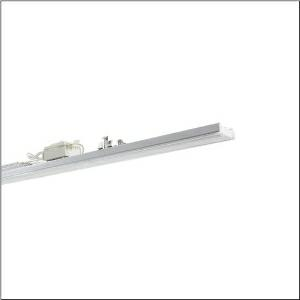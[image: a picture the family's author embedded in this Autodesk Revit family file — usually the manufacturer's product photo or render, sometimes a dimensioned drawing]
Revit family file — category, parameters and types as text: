
# Revit family: licross_r__21_recessed_mo_52tl127n44xg_e1cf
name_source: partatom
category: Lighting Fixtures
units: mm (PartAtom-declared; Revit-internal decimal feet)

## family parameters
Cut with Voids When Loaded = No
Host = Face
Light Source = No
Part Type = Normal
Room Calculation Point = No
Round Connector Dimension = Use Diameter
Shared = No

## types (1)
- Licross® 21 Recessed MO (1 x LED, 4160 lm, 22.2 W, 4000K)
    Apparent Load = 22 VA
    CIE Flux Codes = 72 92 99 100 100
    Color Rendering = 80
    Color Temperature = 4000K
    Default Elevation = 1800 mm
    Description = Licross® 21 Recessed MO, luminaire insert, of sheet steel, galvanised, coil coated, white, length: 1.500mm, width: 66mm, height: 67mm, LED rated luminous flux: 4.160lm, light colour: 840, control gear: ON/OFF, control gear: ECG, with plug, 3-pole, with phase selection, mains connection: 220..240V, AC, 50/60Hz, rated input power: 22W, halogen-free wiring, primary optical cover: cover, of PMMA, light emission: direct distribution, primary light characteristic: symmetric, protection rating (complete): IP40, insulation class (complete): insulation class I (protective earthing), certification: CE, ENEC, VDE, UKCA, protection symbol: D if used in an environment without relevant dust loads with corresponding accessories, impact resistance: IK06, permissible ambient temperature for indoor applications: -35..+50°C, corresponds to IFS (International Featured Standards) requirements for safety and quality in the food industry, reducing of maximum allowable ambient temperature of 5°C with ceiling mounting, LABS conformity tested according to VDMA 24364:2018-05, packaging unit: 1 piece
    Height = 58 mm
    Lamp = 1 x LED
    Lamp Light Flux = 4160 lm
    Lamp Power = 22.2 W
    Lamp count = 1
    Length = 1500 mm
    Luminous efficacy = 187 lm/W
    Manufacturer = Siteco
    ModVariant = No
    Model = 52TL127N44XG
    Mounting Place = Ceiling
    Mounting Type = Pendant
    Number of Poles = 1
    OnlyDefault = Yes
    Power Factor = 1
    Product Name = Licross® 21 Recessed MO
    Product group = luminaire insert
    ProductGroupID = 902
    Protection Class = Protection class I
    Protection Degree = IP 40
    RLX_Detail_Level = 1
    RLX_Emergency_Light_Flux = 0 lm
    RLX_Emergency_Type = 0
    RLX_Emergency_Type_DB = No
    RlxData = <blob elided: 20929 chars, md5=f6171485>
    Socket = socket
    Standby Power = 0 W
    System Light Flux = 4160 lm
    System Power = 22 W
    Type Comments = Product without accessories
    Type Image = l_1296930.jpg
    URL = http://relux.com
    VarID = ---
    Voltage = 0 V
    Weight = 0.00 kg
    Width = 66 mm

## geometry (parser evidence)
native form markers: Blend x4, Sweep x10
no freeform markers — native parametric forms only
